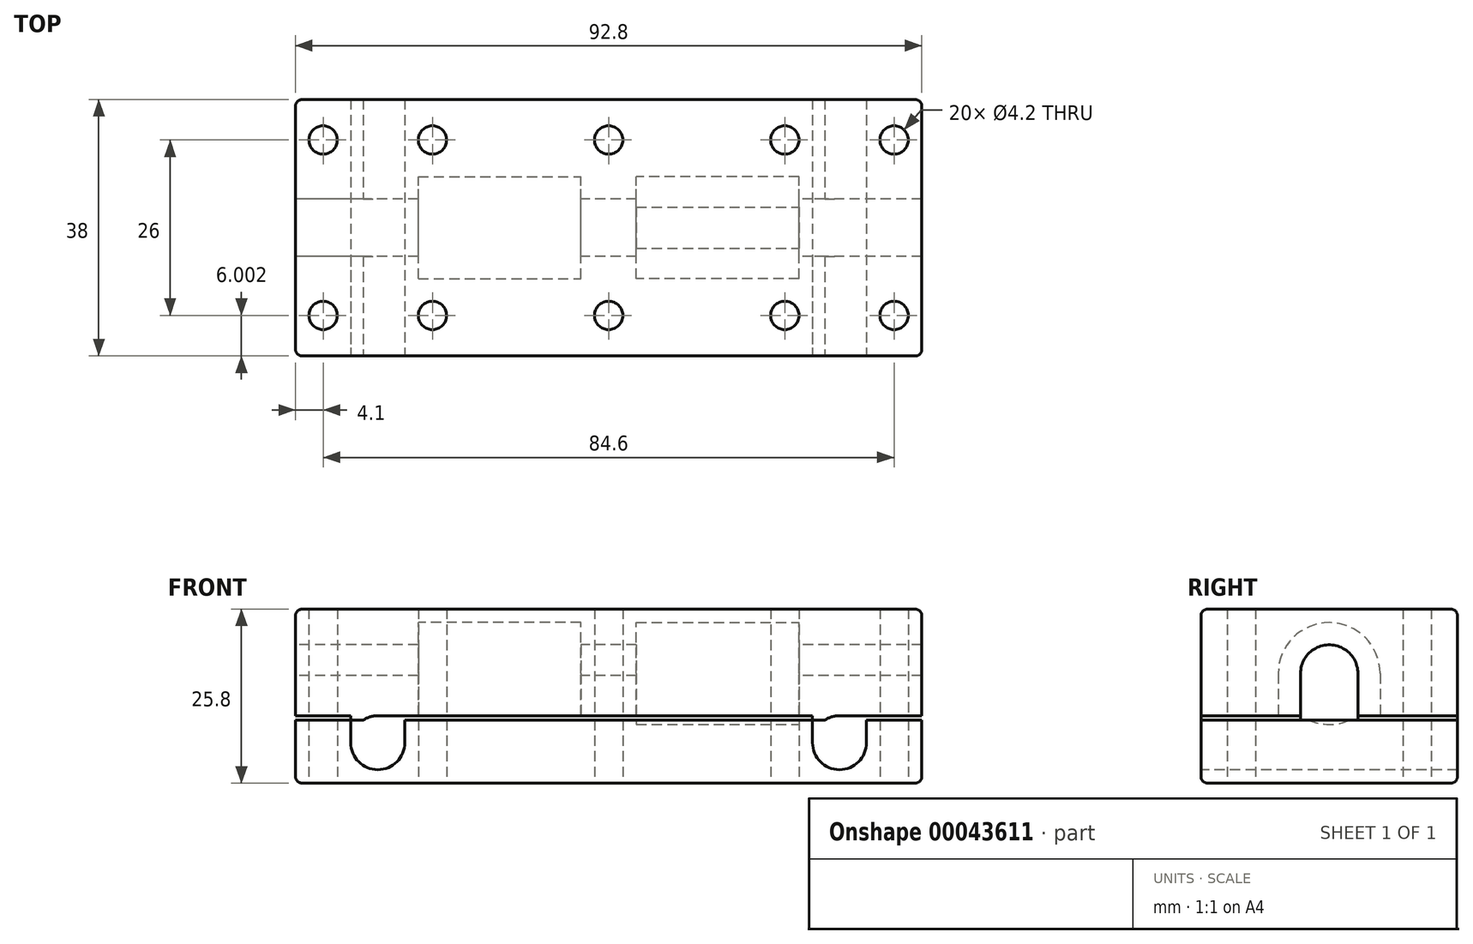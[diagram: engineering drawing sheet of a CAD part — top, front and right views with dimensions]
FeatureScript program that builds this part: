
annotation { "Feature Type Name" : "Feature", "Feature Type Description" : "" }
export const myFeature = defineFeature(function(context is Context, id is Id, definition is map)
    precondition{}
    {
        {
            var Q0;
            Q0=qCreatedBy(makeId("Top.planeOp"),FACE);
            var sketch = newSketch(context, id + "F0", { "sketchPlane" : qUnion([Q0])});
            skLineSegment(sketch, "E0.top", {"start": v(-94.16, -13.28) * mm, "end": v(-47.76, -13.28) * mm});
            skLineSegment(sketch, "E0.left", {"start": v(-94.16, 24.72) * mm, "end": v(-94.16, -13.28) * mm});
            skPoint(sketch, "E1", {"position": v(-94.16, 5.72) * mm});
            skLineSegment(sketch, "E2", {"start": v(-94.16, 5.72) * mm, "end": v(-47.76, 5.72) * mm, "construction": true});
            skPoint(sketch, "E3", {"position": v(-90.06, -13.28) * mm});
            skPoint(sketch, "E4", {"position": v(-81.96, -13.28) * mm});
            skPoint(sketch, "E5", {"position": v(-47.76, -13.28) * mm});
            skLineSegment(sketch, "E6.bottom", {"start": v(-75.96, 13.27) * mm, "end": v(-51.86, 13.27) * mm, "construction": true});
            skLineSegment(sketch, "E6.top", {"start": v(-75.96, -1.83) * mm, "end": v(-51.86, -1.83) * mm, "construction": true});
            skLineSegment(sketch, "E6.left", {"start": v(-75.96, 13.27) * mm, "end": v(-75.96, -1.83) * mm, "construction": true});
            skLineSegment(sketch, "E6.right", {"start": v(-51.86, 13.27) * mm, "end": v(-51.86, -1.83) * mm, "construction": true});
            skLineSegment(sketch, "E7.bottom", {"start": v(-85.96, -13.28) * mm, "end": v(-77.96, -13.28) * mm});
            skLineSegment(sketch, "E7.top", {"start": v(-85.96, 73.63) * mm, "end": v(-77.96, 73.63) * mm});
            skLineSegment(sketch, "E7.left", {"start": v(-85.96, -13.28) * mm, "end": v(-85.96, 73.63) * mm, "construction": true});
            skLineSegment(sketch, "E7.right", {"start": v(-77.96, -13.28) * mm, "end": v(-77.96, 73.63) * mm, "construction": true});
            skLineSegment(sketch, "E8", {"start": v(-47.76, -13.28) * mm, "end": v(-47.76, 24.72) * mm});
            skLineSegment(sketch, "E9", {"start": v(-94.16, 24.72) * mm, "end": v(-47.76, 24.72) * mm});
            skLineSegment(sketch, "E10.MirrorCS", {"start": v(-9.56, 73.63) * mm, "end": v(-17.56, 73.63) * mm});
            skLineSegment(sketch, "E11.MirrorCS", {"start": v(-9.56, -13.28) * mm, "end": v(-17.56, -13.28) * mm});
            skLineSegment(sketch, "E12.MirrorCS", {"start": v(-17.56, -13.28) * mm, "end": v(-17.56, 73.63) * mm, "construction": true});
            skLineSegment(sketch, "E13.MirrorCS", {"start": v(-1.36, 24.72) * mm, "end": v(-47.76, 24.72) * mm});
            skLineSegment(sketch, "E14.MirrorCS", {"start": v(-9.56, -13.28) * mm, "end": v(-9.56, 73.63) * mm, "construction": true});
            skPoint(sketch, "E15.MirrorP", {"position": v(-5.46, -13.28) * mm});
            skPoint(sketch, "E16.MirrorP", {"position": v(-13.56, -13.28) * mm});
            skLineSegment(sketch, "E17.MirrorCS", {"start": v(-1.36, 5.72) * mm, "end": v(-47.76, 5.72) * mm, "construction": true});
            skLineSegment(sketch, "E18.MirrorCS", {"start": v(-19.56, 13.27) * mm, "end": v(-43.66, 13.27) * mm, "construction": true});
            skLineSegment(sketch, "E19.MirrorCS", {"start": v(-19.56, -1.83) * mm, "end": v(-43.66, -1.83) * mm, "construction": true});
            skLineSegment(sketch, "E20.MirrorCS", {"start": v(-19.56, 13.27) * mm, "end": v(-19.56, -1.83) * mm, "construction": true});
            skLineSegment(sketch, "E21.MirrorCS", {"start": v(-43.66, 13.27) * mm, "end": v(-43.66, -1.83) * mm, "construction": true});
            skPoint(sketch, "E22.MirrorP", {"position": v(-1.36, 5.72) * mm});
            skLineSegment(sketch, "E23.MirrorCS", {"start": v(-1.36, -13.28) * mm, "end": v(-47.76, -13.28) * mm});
            skLineSegment(sketch, "E24.MirrorCS", {"start": v(-1.36, 24.72) * mm, "end": v(-1.36, -13.28) * mm});
            skPoint(sketch, "E25", {"position": v(-90.06, 18.72) * mm});
            skPoint(sketch, "E26", {"position": v(-47.76, 18.72) * mm});
            skPoint(sketch, "E27", {"position": v(-5.46, 18.72) * mm});
            skPoint(sketch, "E28", {"position": v(-5.46, -7.28) * mm});
            skPoint(sketch, "E29", {"position": v(-47.76, -7.28) * mm});
            skPoint(sketch, "E30", {"position": v(-90.06, -7.28) * mm});
            skLineSegment(sketch, "E31", {"start": v(-76.94, 18.72) * mm, "end": v(-49.91, 18.72) * mm, "construction": true});
            skPoint(sketch, "E32", {"position": v(-73.86, 18.72) * mm});
            skPoint(sketch, "E33", {"position": v(-21.66, 18.72) * mm});
            skPoint(sketch, "E34", {"position": v(-73.86, -7.28) * mm});
            skPoint(sketch, "E35", {"position": v(-21.66, -7.28) * mm});
            skSolve(sketch);
        }
        {
            var Q0;
            {var subQ1=sQuery(id+"F0.wireOp",EDGE,"E0.left");Q0=makeQuery(id+"F0.imprint","IMPRINT",FACE,{"disambiguationData":[TD([[makeQuery(id+"F0.imprint","IMPRINT",EDGE,{"derivedFrom":subQ1}),1.0]])]});}
            var Q1;
            {var subQ0=sQuery(id+"F0.wireOp",EDGE,"E8");Q1=makeQuery(id+"F0.imprint","IMPRINT",FACE,{"disambiguationData":[TD([[makeQuery(id+"F0.imprint","IMPRINT",EDGE,{"derivedFrom":subQ0}),-1.0]])]});}
            extrude(context, id + "F1", {"entities" : qUnion([Q0, Q1]), "depth" : 25.8 * mm});
        }
        {
            var Q0;
            Q0=makeQuery(id+"F1.opExtrude","SWEPT_FACE",FACE,{"disambiguationData":[OSD([sQuery(id+"F0.wireOp",EDGE,"E0.left")])]});
            var sketch = newSketch(context, id + "F2", { "sketchPlane" : qUnion([Q0])});
            skPoint(sketch, "E36", {"position": v(-5.72, 16.25) * mm});
            skCircle(sketch, "E37", {"center": v(-5.72, 16.25) * mm, "radius": 4.25 * mm});
            skCircle(sketch, "E38", {"center": v(-5.72, 16.25) * mm, "radius": 7.55 * mm});
            skLineSegment(sketch, "E39", {"start": v(-24.72, 9.35) * mm, "end": v(13.28, 9.35) * mm});
            skLineSegment(sketch, "E40", {"start": v(-9.96, 15.96) * mm, "end": v(-9.96, 9.35) * mm});
            skLineSegment(sketch, "E41", {"start": v(-1.47, 16.25) * mm, "end": v(-1.47, 9.35) * mm});
            skPoint(sketch, "E42", {"position": v(-24.72, -4.75) * mm});
            skPoint(sketch, "E43", {"position": v(-24.72, -16.75) * mm});
            skSolve(sketch);
        }
        {
            var Q0;
            Q0=makeQuery(id+"F1.opExtrude","SWEPT_FACE",FACE,{"disambiguationData":[OSD([sQuery(id+"F0.wireOp",EDGE,"E0.top"),sQuery(id+"F0.wireOp",EDGE,"E7.bottom"),sQuery(id+"F0.wireOp",EDGE,"E23.MirrorCS")])]});
            var sketch = newSketch(context, id + "F3", { "sketchPlane" : qUnion([Q0])});
            skPoint(sketch, "E44", {"position": v(-81.96, 6) * mm});
            skCircle(sketch, "E45", {"center": v(-81.96, 6) * mm, "radius": 4 * mm});
            skPoint(sketch, "E46", {"position": v(-13.56, 6) * mm});
            skCircle(sketch, "E47", {"center": v(-13.56, 6) * mm, "radius": 4 * mm});
            skLineSegment(sketch, "E48.bottom", {"start": v(-94.16, 10) * mm, "end": v(-1.36, 10) * mm});
            skLineSegment(sketch, "E48.top", {"start": v(-94.16, 9.35) * mm, "end": v(-1.36, 9.35) * mm});
            skLineSegment(sketch, "E48.left", {"start": v(-94.16, 10) * mm, "end": v(-94.16, 9.35) * mm});
            skLineSegment(sketch, "E48.right", {"start": v(-1.36, 10) * mm, "end": v(-1.36, 9.35) * mm});
            skLineSegment(sketch, "E49.bottom", {"start": v(-85.96, 6) * mm, "end": v(-77.96, 6) * mm});
            skLineSegment(sketch, "E49.top", {"start": v(-85.96, 10) * mm, "end": v(-77.96, 10) * mm});
            skLineSegment(sketch, "E49.left", {"start": v(-85.96, 6) * mm, "end": v(-85.96, 10) * mm});
            skLineSegment(sketch, "E49.right", {"start": v(-77.96, 6) * mm, "end": v(-77.96, 10) * mm});
            skLineSegment(sketch, "E50.bottom", {"start": v(-17.56, 6) * mm, "end": v(-9.56, 6) * mm});
            skLineSegment(sketch, "E50.top", {"start": v(-17.56, 10) * mm, "end": v(-9.56, 10) * mm});
            skLineSegment(sketch, "E50.left", {"start": v(-17.56, 6) * mm, "end": v(-17.56, 10) * mm});
            skLineSegment(sketch, "E50.right", {"start": v(-9.56, 6) * mm, "end": v(-9.56, 10) * mm});
            skSolve(sketch);
        }
        {
            var Q0;
            Q0=makeQuery(id+"F2.imprint","IMPRINT",FACE,{"disambiguationData":[TD([[makeQuery(id+"F2.imprint","IMPRINT",EDGE,{"derivedFrom":sQuery(id+"F2.wireOp",EDGE,"E37")}),1.0]])]});
            var Q1;
            {var subQ6=sQuery(id+"F2.wireOp",EDGE,"E40");var subQ8=sQuery(id+"F2.wireOp",EDGE,"E37");var subQ9=makeQuery(id+"F2.imprint","INTERSECT",VERTEX,{"derivedFrom":[subQ8,subQ6]});Q1=makeQuery(id+"F2.imprint","IMPRINT",FACE,{"disambiguationData":[TD([[makeQuery(id+"F2.imprint","IMPRINT",EDGE,{"disambiguationData":[TD([[subQ9,-1.0]])],"derivedFrom":subQ8}),-1.0]])]});}
            var Q2;
            {var subQ0=sQuery(id+"F2.wireOp",EDGE,"E39");var subQ1=sQuery(id+"F2.wireOp",EDGE,"E38");var subQ2=makeQuery(id+"F2.imprint","INTERSECT",VERTEX,{"disambiguationData":[OD(0.0)],"derivedFrom":[subQ1,subQ0]});Q2=makeQuery(id+"F2.imprint","IMPRINT",FACE,{"disambiguationData":[TD([[makeQuery(id+"F2.imprint","IMPRINT",EDGE,{"disambiguationData":[TD([[subQ2,1.0]])],"derivedFrom":subQ1}),-1.0]])]});}
            var Q3;
            {var subQ0=sQuery(id+"F2.wireOp",EDGE,"E39");var subQ1=sQuery(id+"F2.wireOp",EDGE,"E38");var subQ2=makeQuery(id+"F2.imprint","INTERSECT",VERTEX,{"disambiguationData":[OD(1.0)],"derivedFrom":[subQ1,subQ0]});Q3=makeQuery(id+"F2.imprint","IMPRINT",FACE,{"disambiguationData":[TD([[makeQuery(id+"F2.imprint","IMPRINT",EDGE,{"disambiguationData":[TD([[subQ2,-1.0]])],"derivedFrom":subQ1}),-1.0]])]});}
            extrude(context, id + "F4", {"entities" : qUnion([Q0, Q1, Q2, Q3]), "operationType" : NewBodyOperationType.REMOVE, "endBound" : BoundingType.THROUGH_ALL, "oppositeDirection" : true, "depth" : 25 * mm});
        }
        {
            var Q0;
            Q0=makeQuery(id+"F3.imprint","IMPRINT",FACE,{"disambiguationData":[TD([[makeQuery(id+"F3.imprint","IMPRINT",EDGE,{"derivedFrom":sQuery(id+"F3.wireOp",EDGE,"E45")}),1.0]])]});
            var Q1;
            Q1=makeQuery(id+"F3.imprint","IMPRINT",FACE,{"disambiguationData":[TD([[makeQuery(id+"F3.imprint","IMPRINT",EDGE,{"derivedFrom":sQuery(id+"F3.wireOp",EDGE,"E47")}),1.0]])]});
            var Q2;
            {var subQ0=sQuery(id+"F3.wireOp",EDGE,"E49.bottom");Q2=makeQuery(id+"F3.imprint","IMPRINT",FACE,{"disambiguationData":[TD([[makeQuery(id+"F3.imprint","IMPRINT",EDGE,{"derivedFrom":subQ0}),1.0]])]});}
            var Q3;
            {var subQ0=sQuery(id+"F3.wireOp",EDGE,"E49.bottom");Q3=makeQuery(id+"F3.imprint","IMPRINT",FACE,{"disambiguationData":[TD([[makeQuery(id+"F3.imprint","IMPRINT",EDGE,{"derivedFrom":subQ0}),-1.0]])]});}
            var Q4;
            {var subQ1=sQuery(id+"F3.wireOp",EDGE,"E45");var subQ3=sQuery(id+"F3.wireOp",EDGE,"E48.top");var subQ4=makeQuery(id+"F3.imprint","INTERSECT",VERTEX,{"disambiguationData":[OD(0.0)],"derivedFrom":[subQ1,subQ3]});Q4=makeQuery(id+"F3.imprint","IMPRINT",FACE,{"disambiguationData":[TD([[makeQuery(id+"F3.imprint","IMPRINT",EDGE,{"disambiguationData":[TD([[subQ4,-1.0]])],"derivedFrom":subQ3}),-1.0]])]});}
            var Q5;
            {var subQ0=sQuery(id+"F3.wireOp",EDGE,"E48.top");var subQ1=sQuery(id+"F3.wireOp",EDGE,"E45");var subQ2=makeQuery(id+"F3.imprint","INTERSECT",VERTEX,{"disambiguationData":[OD(0.0)],"derivedFrom":[subQ1,subQ0]});Q5=makeQuery(id+"F3.imprint","IMPRINT",FACE,{"disambiguationData":[TD([[makeQuery(id+"F3.imprint","IMPRINT",EDGE,{"disambiguationData":[TD([[subQ2,-1.0]])],"derivedFrom":subQ1}),-1.0]])]});}
            var Q6;
            {var subQ0=sQuery(id+"F3.wireOp",EDGE,"E49.top");var subQ1=sQuery(id+"F3.wireOp",EDGE,"E45");var subQ2=makeQuery(id+"F3.imprint","INTERSECT",VERTEX,{"derivedFrom":[subQ1,subQ0]});Q6=makeQuery(id+"F3.imprint","IMPRINT",FACE,{"disambiguationData":[TD([[makeQuery(id+"F3.imprint","IMPRINT",EDGE,{"disambiguationData":[TD([[subQ2,-1.0]])],"derivedFrom":subQ1}),-1.0]])]});}
            var Q7;
            {var subQ1=sQuery(id+"F3.wireOp",EDGE,"E45");var subQ3=sQuery(id+"F3.wireOp",EDGE,"E48.top");var subQ4=makeQuery(id+"F3.imprint","INTERSECT",VERTEX,{"disambiguationData":[OD(1.0)],"derivedFrom":[subQ1,subQ3]});Q7=makeQuery(id+"F3.imprint","IMPRINT",FACE,{"disambiguationData":[TD([[makeQuery(id+"F3.imprint","IMPRINT",EDGE,{"disambiguationData":[TD([[subQ4,1.0]])],"derivedFrom":subQ3}),-1.0]])]});}
            var Q8;
            {var subQ0=sQuery(id+"F3.wireOp",EDGE,"E50.bottom");Q8=makeQuery(id+"F3.imprint","IMPRINT",FACE,{"disambiguationData":[TD([[makeQuery(id+"F3.imprint","IMPRINT",EDGE,{"derivedFrom":subQ0}),1.0]])]});}
            var Q9;
            {var subQ0=sQuery(id+"F3.wireOp",EDGE,"E50.bottom");Q9=makeQuery(id+"F3.imprint","IMPRINT",FACE,{"disambiguationData":[TD([[makeQuery(id+"F3.imprint","IMPRINT",EDGE,{"derivedFrom":subQ0}),-1.0]])]});}
            var Q10;
            {var subQ0=sQuery(id+"F3.wireOp",EDGE,"E50.top");var subQ1=sQuery(id+"F3.wireOp",EDGE,"E47");var subQ2=makeQuery(id+"F3.imprint","INTERSECT",VERTEX,{"derivedFrom":[subQ1,subQ0]});Q10=makeQuery(id+"F3.imprint","IMPRINT",FACE,{"disambiguationData":[TD([[makeQuery(id+"F3.imprint","IMPRINT",EDGE,{"disambiguationData":[TD([[subQ2,-1.0]])],"derivedFrom":subQ1}),-1.0]])]});}
            var Q11;
            {var subQ1=sQuery(id+"F3.wireOp",EDGE,"E47");var subQ3=sQuery(id+"F3.wireOp",EDGE,"E48.top");var subQ4=makeQuery(id+"F3.imprint","INTERSECT",VERTEX,{"disambiguationData":[OD(1.0)],"derivedFrom":[subQ1,subQ3]});Q11=makeQuery(id+"F3.imprint","IMPRINT",FACE,{"disambiguationData":[TD([[makeQuery(id+"F3.imprint","IMPRINT",EDGE,{"disambiguationData":[TD([[subQ4,1.0]])],"derivedFrom":subQ3}),-1.0]])]});}
            var Q12;
            {var subQ1=sQuery(id+"F3.wireOp",EDGE,"E47");var subQ3=sQuery(id+"F3.wireOp",EDGE,"E48.top");var subQ4=makeQuery(id+"F3.imprint","INTERSECT",VERTEX,{"disambiguationData":[OD(0.0)],"derivedFrom":[subQ1,subQ3]});Q12=makeQuery(id+"F3.imprint","IMPRINT",FACE,{"disambiguationData":[TD([[makeQuery(id+"F3.imprint","IMPRINT",EDGE,{"disambiguationData":[TD([[subQ4,-1.0]])],"derivedFrom":subQ3}),-1.0]])]});}
            var Q13;
            {var subQ0=sQuery(id+"F3.wireOp",EDGE,"E48.top");var subQ1=sQuery(id+"F3.wireOp",EDGE,"E47");var subQ2=makeQuery(id+"F3.imprint","INTERSECT",VERTEX,{"disambiguationData":[OD(0.0)],"derivedFrom":[subQ1,subQ0]});Q13=makeQuery(id+"F3.imprint","IMPRINT",FACE,{"disambiguationData":[TD([[makeQuery(id+"F3.imprint","IMPRINT",EDGE,{"disambiguationData":[TD([[subQ2,-1.0]])],"derivedFrom":subQ1}),-1.0]])]});}
            var Q14;
            {var subQ0=sQuery(id+"F3.wireOp",EDGE,"E49.right");var subQ5=sQuery(id+"F3.wireOp",EDGE,"E48.top");var subQ6=makeQuery(id+"F3.imprint","INTERSECT",VERTEX,{"derivedFrom":[subQ5,subQ0]});Q14=makeQuery(id+"F3.imprint","IMPRINT",FACE,{"disambiguationData":[TD([[makeQuery(id+"F3.imprint","IMPRINT",EDGE,{"disambiguationData":[TD([[subQ6,-1.0]])],"derivedFrom":subQ5}),1.0]])]});}
            var Q15;
            {var subQ0=sQuery(id+"F3.wireOp",EDGE,"E48.left");Q15=makeQuery(id+"F3.imprint","IMPRINT",FACE,{"disambiguationData":[TD([[makeQuery(id+"F3.imprint","IMPRINT",EDGE,{"derivedFrom":subQ0}),1.0]])]});}
            var Q16;
            {var subQ0=sQuery(id+"F3.wireOp",EDGE,"E48.right");Q16=makeQuery(id+"F3.imprint","IMPRINT",FACE,{"disambiguationData":[TD([[makeQuery(id+"F3.imprint","IMPRINT",EDGE,{"derivedFrom":subQ0}),-1.0]])]});}
            extrude(context, id + "F5", {"entities" : qUnion([Q0, Q1, Q2, Q3, Q4, Q5, Q6, Q7, Q8, Q9, Q10, Q11, Q12, Q13, Q14, Q15, Q16]), "operationType" : NewBodyOperationType.REMOVE, "endBound" : BoundingType.THROUGH_ALL, "oppositeDirection" : true, "depth" : 25 * mm});
        }
        {
            var Q0;
            Q0=sQuery(id+"F0.wireOp",EDGE,"E6.left");
            var Q1;
            Q1=qCreatedBy(makeId("Right.planeOp"),FACE);
            cPlane(context, id + "F6", {"entities" : qUnion([Q0, Q1]), "cplaneType" : CPlaneType.LINE_ANGLE, "offset" : 25 * mm, "angle" : 0 * degree, "width" : 150 * mm, "height" : 150 * mm});
        }
        {
            var Q0;
            Q0=qCreatedBy(id+"F6.planeOp",FACE);
            var sketch = newSketch(context, id + "F7", { "sketchPlane" : qUnion([Q0])});
            skCircle(sketch, "E51", {"center": v(-5.72, 16.25) * mm, "radius": 7.55 * mm});
            skLineSegment(sketch, "E52.bottom", {"start": v(-13.27, 16.25) * mm, "end": v(1.83, 16.25) * mm});
            skLineSegment(sketch, "E52.top", {"start": v(-13.27, 9.35) * mm, "end": v(1.83, 9.35) * mm});
            skLineSegment(sketch, "E52.left", {"start": v(-13.27, 16.25) * mm, "end": v(-13.27, 9.35) * mm});
            skLineSegment(sketch, "E52.right", {"start": v(1.83, 16.25) * mm, "end": v(1.83, 9.35) * mm});
            skSolve(sketch);
        }
        {
            var Q0;
            {var subQ0=sQuery(id+"F7.wireOp",EDGE,"E52.left");Q0=makeQuery(id+"F7.imprint","IMPRINT",FACE,{"disambiguationData":[TD([[makeQuery(id+"F7.imprint","IMPRINT",EDGE,{"derivedFrom":subQ0}),1.0]])]});}
            var Q1;
            {var subQ0=sQuery(id+"F7.wireOp",EDGE,"E52.right");Q1=makeQuery(id+"F7.imprint","IMPRINT",FACE,{"disambiguationData":[TD([[makeQuery(id+"F7.imprint","IMPRINT",EDGE,{"derivedFrom":subQ0}),-1.0]])]});}
            var Q2;
            {var subQ0=sQuery(id+"F7.wireOp",EDGE,"E52.bottom");Q2=makeQuery(id+"F7.imprint","IMPRINT",FACE,{"disambiguationData":[TD([[makeQuery(id+"F7.imprint","IMPRINT",EDGE,{"derivedFrom":subQ0}),-1.0]])]});}
            var Q3;
            {var subQ0=sQuery(id+"F7.wireOp",EDGE,"E52.bottom");Q3=makeQuery(id+"F7.imprint","IMPRINT",FACE,{"disambiguationData":[TD([[makeQuery(id+"F7.imprint","IMPRINT",EDGE,{"derivedFrom":subQ0}),1.0]])]});}
            var Q4;
            {var subQ0=sQuery(id+"F7.wireOp",EDGE,"E52.top");var subQ1=sQuery(id+"F7.wireOp",EDGE,"E51");var subQ2=makeQuery(id+"F7.imprint","INTERSECT",VERTEX,{"disambiguationData":[OD(0.0)],"derivedFrom":[subQ1,subQ0]});Q4=makeQuery(id+"F7.imprint","IMPRINT",FACE,{"disambiguationData":[TD([[makeQuery(id+"F7.imprint","IMPRINT",EDGE,{"disambiguationData":[TD([[subQ2,-1.0]])],"derivedFrom":subQ1}),1.0]])]});}
            extrude(context, id + "F8", {"entities" : qUnion([Q0, Q1, Q2, Q3, Q4]), "operationType" : NewBodyOperationType.REMOVE, "oppositeDirection" : true, "depth" : 24.1 * mm});
        }
        {
            var Q0;
            Q0=sQuery(id+"F0.wireOp",EDGE,"E20.MirrorCS");
            var Q1;
            Q1=qCreatedBy(makeId("Right.planeOp"),FACE);
            cPlane(context, id + "F9", {"entities" : qUnion([Q0, Q1]), "cplaneType" : CPlaneType.LINE_ANGLE, "offset" : 25 * mm, "angle" : 0 * degree, "width" : 150 * mm, "height" : 150 * mm});
        }
        {
            var Q0;
            Q0=qCreatedBy(id+"F9.planeOp",FACE);
            var sketch = newSketch(context, id + "F10", { "sketchPlane" : qUnion([Q0])});
            skPoint(sketch, "E53", {"position": v(-5.72, 16.25) * mm});
            skCircle(sketch, "E54", {"center": v(-5.72, 16.25) * mm, "radius": 7.55 * mm});
            skLineSegment(sketch, "E55.bottom", {"start": v(1.83, 16.25) * mm, "end": v(-13.27, 16.25) * mm});
            skLineSegment(sketch, "E55.top", {"start": v(1.83, 9.35) * mm, "end": v(-13.27, 9.35) * mm});
            skLineSegment(sketch, "E55.left", {"start": v(1.83, 16.25) * mm, "end": v(1.83, 9.35) * mm});
            skLineSegment(sketch, "E55.right", {"start": v(-13.27, 16.25) * mm, "end": v(-13.27, 9.35) * mm});
            skSolve(sketch);
        }
        {
            var Q0;
            {var subQ0=sQuery(id+"F10.wireOp",EDGE,"E55.bottom");Q0=makeQuery(id+"F10.imprint","IMPRINT",FACE,{"disambiguationData":[TD([[makeQuery(id+"F10.imprint","IMPRINT",EDGE,{"derivedFrom":subQ0}),-1.0]])]});}
            var Q1;
            {var subQ0=sQuery(id+"F10.wireOp",EDGE,"E55.bottom");Q1=makeQuery(id+"F10.imprint","IMPRINT",FACE,{"disambiguationData":[TD([[makeQuery(id+"F10.imprint","IMPRINT",EDGE,{"derivedFrom":subQ0}),1.0]])]});}
            var Q2;
            {var subQ0=sQuery(id+"F10.wireOp",EDGE,"E55.right");Q2=makeQuery(id+"F10.imprint","IMPRINT",FACE,{"disambiguationData":[TD([[makeQuery(id+"F10.imprint","IMPRINT",EDGE,{"derivedFrom":subQ0}),1.0]])]});}
            var Q3;
            {var subQ0=sQuery(id+"F10.wireOp",EDGE,"E55.left");Q3=makeQuery(id+"F10.imprint","IMPRINT",FACE,{"disambiguationData":[TD([[makeQuery(id+"F10.imprint","IMPRINT",EDGE,{"derivedFrom":subQ0}),-1.0]])]});}
            var Q4;
            {var subQ0=sQuery(id+"F10.wireOp",EDGE,"E55.top");var subQ1=sQuery(id+"F10.wireOp",EDGE,"E54");var subQ2=makeQuery(id+"F10.imprint","INTERSECT",VERTEX,{"disambiguationData":[OD(0.0)],"derivedFrom":[subQ1,subQ0]});Q4=makeQuery(id+"F10.imprint","IMPRINT",FACE,{"disambiguationData":[TD([[makeQuery(id+"F10.imprint","IMPRINT",EDGE,{"disambiguationData":[TD([[subQ2,-1.0]])],"derivedFrom":subQ1}),1.0]])]});}
            extrude(context, id + "F11", {"entities" : qUnion([Q0, Q1, Q2, Q3, Q4]), "operationType" : NewBodyOperationType.REMOVE, "depth" : 24.1 * mm});
        }
        {
            var Q0;
            Q0=makeQuery(id+"F1.opExtrude","CAP_EDGE",EDGE,{"disambiguationData":[OSD([sQuery(id+"F0.wireOp",EDGE,"E0.top"),sQuery(id+"F0.wireOp",EDGE,"E7.bottom"),sQuery(id+"F0.wireOp",EDGE,"E23.MirrorCS")])],"isStart":true});
            var Q1;
            Q1=makeQuery(id+"F1.opExtrude","CAP_EDGE",EDGE,{"disambiguationData":[OSD([sQuery(id+"F0.wireOp",EDGE,"E24.MirrorCS")])],"isStart":true});
            var Q2;
            Q2=makeQuery(id+"F1.opExtrude","CAP_EDGE",EDGE,{"disambiguationData":[OSD([sQuery(id+"F0.wireOp",EDGE,"E0.left")])],"isStart":true});
            var Q3;
            Q3=makeQuery(id+"F1.opExtrude","CAP_EDGE",EDGE,{"disambiguationData":[OSD([sQuery(id+"F0.wireOp",EDGE,"E9"),sQuery(id+"F0.wireOp",EDGE,"E13.MirrorCS")])],"isStart":false});
            var Q4;
            Q4=makeQuery(id+"F1.opExtrude","CAP_EDGE",EDGE,{"disambiguationData":[OSD([sQuery(id+"F0.wireOp",EDGE,"E0.top"),sQuery(id+"F0.wireOp",EDGE,"E7.bottom"),sQuery(id+"F0.wireOp",EDGE,"E23.MirrorCS")])],"isStart":false});
            var Q5;
            Q5=makeQuery(id+"F1.opExtrude","CAP_EDGE",EDGE,{"disambiguationData":[OSD([sQuery(id+"F0.wireOp",EDGE,"E24.MirrorCS")])],"isStart":false});
            var Q6;
            {var subQ0=sQuery(id+"F0.wireOp",EDGE,"E24.MirrorCS");var subQ1=sQuery(id+"F0.wireOp",EDGE,"E13.MirrorCS");Q6=makeQuery(id+"F5.boolean.opBoolean","SPLIT",EDGE,{"disambiguationData":[TD([makeQuery(id+"F5.opExtrude","SWEPT_FACE",FACE,{"disambiguationData":[OSD([sQuery(id+"F3.wireOp",EDGE,"E48.bottom"),sQuery(id+"F3.wireOp",EDGE,"E49.top"),sQuery(id+"F3.wireOp",EDGE,"E50.top")])]})])],"derivedFrom":makeQuery(id+"F1.opExtrude","SWEPT_EDGE",EDGE,{"disambiguationData":[OSD([subQ1,subQ0])]})});}
            var Q7;
            {var subQ0=sQuery(id+"F0.wireOp",EDGE,"E24.MirrorCS");var subQ1=sQuery(id+"F0.wireOp",EDGE,"E23.MirrorCS");Q7=makeQuery(id+"F5.boolean.opBoolean","SPLIT",EDGE,{"disambiguationData":[TD([makeQuery(id+"F5.opExtrude","SWEPT_FACE",FACE,{"disambiguationData":[OSD([sQuery(id+"F3.wireOp",EDGE,"E48.bottom"),sQuery(id+"F3.wireOp",EDGE,"E49.top"),sQuery(id+"F3.wireOp",EDGE,"E50.top")])]})])],"derivedFrom":makeQuery(id+"F1.opExtrude","SWEPT_EDGE",EDGE,{"disambiguationData":[OSD([subQ1,subQ0])]})});}
            var Q8;
            {var subQ0=sQuery(id+"F0.wireOp",EDGE,"E24.MirrorCS");var subQ1=sQuery(id+"F0.wireOp",EDGE,"E23.MirrorCS");var subQ5=makeQuery(id+"F1.opExtrude","SWEPT_EDGE",EDGE,{"disambiguationData":[OSD([subQ1,subQ0])]});Q8=makeQuery(id+"F5.boolean.opBoolean","SPLIT",EDGE,{"disambiguationData":[TD([makeQuery(id+"F4.boolean.opBoolean","COPY",FACE,{"derivedFrom":makeQuery(id+"F4.opExtrude","SWEPT_FACE",FACE,{"disambiguationData":[OSD([sQuery(id+"F2.wireOp",EDGE,"E39")])]})})])],"derivedFrom":subQ5});}
            var Q9;
            {var subQ0=sQuery(id+"F0.wireOp",EDGE,"E24.MirrorCS");var subQ1=sQuery(id+"F0.wireOp",EDGE,"E13.MirrorCS");Q9=makeQuery(id+"F5.boolean.opBoolean","SPLIT",EDGE,{"disambiguationData":[TD([makeQuery(id+"F4.boolean.opBoolean","COPY",FACE,{"derivedFrom":makeQuery(id+"F4.opExtrude","SWEPT_FACE",FACE,{"disambiguationData":[OSD([sQuery(id+"F2.wireOp",EDGE,"E39")])]})})])],"derivedFrom":makeQuery(id+"F1.opExtrude","SWEPT_EDGE",EDGE,{"disambiguationData":[OSD([subQ1,subQ0])]})});}
            var Q10;
            Q10=makeQuery(id+"F1.opExtrude","CAP_EDGE",EDGE,{"disambiguationData":[OSD([sQuery(id+"F0.wireOp",EDGE,"E0.left")])],"isStart":false});
            var Q11;
            {var subQ2=sQuery(id+"F0.wireOp",EDGE,"E0.left");var subQ3=sQuery(id+"F0.wireOp",EDGE,"E0.top");Q11=makeQuery(id+"F5.boolean.opBoolean","SPLIT",EDGE,{"disambiguationData":[TD([makeQuery(id+"F5.opExtrude","SWEPT_FACE",FACE,{"disambiguationData":[OSD([sQuery(id+"F3.wireOp",EDGE,"E48.bottom"),sQuery(id+"F3.wireOp",EDGE,"E49.top"),sQuery(id+"F3.wireOp",EDGE,"E50.top")])]})])],"derivedFrom":makeQuery(id+"F1.opExtrude","SWEPT_EDGE",EDGE,{"disambiguationData":[OSD([subQ3,subQ2])]})});}
            var Q12;
            {var subQ0=sQuery(id+"F0.wireOp",EDGE,"E0.left");var subQ3=sQuery(id+"F0.wireOp",EDGE,"E0.top");var subQ5=makeQuery(id+"F1.opExtrude","SWEPT_EDGE",EDGE,{"disambiguationData":[OSD([subQ3,subQ0])]});Q12=makeQuery(id+"F5.boolean.opBoolean","SPLIT",EDGE,{"disambiguationData":[TD([makeQuery(id+"F4.boolean.opBoolean","COPY",FACE,{"derivedFrom":makeQuery(id+"F4.opExtrude","SWEPT_FACE",FACE,{"disambiguationData":[OSD([sQuery(id+"F2.wireOp",EDGE,"E39")])]})})])],"derivedFrom":subQ5});}
            var Q13;
            {var subQ1=sQuery(id+"F0.wireOp",EDGE,"E9");var subQ3=sQuery(id+"F0.wireOp",EDGE,"E0.left");Q13=makeQuery(id+"F5.boolean.opBoolean","SPLIT",EDGE,{"disambiguationData":[TD([makeQuery(id+"F4.boolean.opBoolean","COPY",FACE,{"derivedFrom":makeQuery(id+"F4.opExtrude","SWEPT_FACE",FACE,{"disambiguationData":[OSD([sQuery(id+"F2.wireOp",EDGE,"E39")])]})})])],"derivedFrom":makeQuery(id+"F1.opExtrude","SWEPT_EDGE",EDGE,{"disambiguationData":[OSD([subQ3,subQ1])]})});}
            var Q14;
            {var subQ1=sQuery(id+"F0.wireOp",EDGE,"E9");var subQ2=sQuery(id+"F0.wireOp",EDGE,"E0.left");Q14=makeQuery(id+"F5.boolean.opBoolean","SPLIT",EDGE,{"disambiguationData":[TD([makeQuery(id+"F5.opExtrude","SWEPT_FACE",FACE,{"disambiguationData":[OSD([sQuery(id+"F3.wireOp",EDGE,"E48.bottom"),sQuery(id+"F3.wireOp",EDGE,"E49.top"),sQuery(id+"F3.wireOp",EDGE,"E50.top")])]})])],"derivedFrom":makeQuery(id+"F1.opExtrude","SWEPT_EDGE",EDGE,{"disambiguationData":[OSD([subQ2,subQ1])]})});}
            var Q15;
            {var subQ1=sQuery(id+"F0.wireOp",EDGE,"E24.MirrorCS");var subQ2=sQuery(id+"F0.wireOp",EDGE,"E13.MirrorCS");var subQ3=sQuery(id+"F0.wireOp",EDGE,"E9");Q15=makeQuery(id+"FaV5U625bywUatc_3.opBoolean","SPLIT",EDGE,{"disambiguationData":[TD([makeQuery(id+"F1.opExtrude","SWEPT_FACE",FACE,{"disambiguationData":[OSD([subQ1])]})])],"derivedFrom":makeQuery(id+"F1.opExtrude","CAP_EDGE",EDGE,{"disambiguationData":[OSD([subQ3,subQ2])],"isStart":true})});}
            var Q16;
            {var subQ0=sQuery(id+"Fnf9aDBOugkyyxO_1.wireOp",EDGE,"qgUEgUuF-Gk1c-hbKn-L9CV-MhQixRefJ1HH.right");var subQ1=sQuery(id+"F0.wireOp",EDGE,"E13.MirrorCS");var subQ2=sQuery(id+"F0.wireOp",EDGE,"E9");Q16=makeQuery(id+"FaV5U625bywUatc_3.opBoolean","SPLIT",EDGE,{"disambiguationData":[TD([makeQuery(id+"Fpmijf7J7eOStOP_1.opExtrude","SWEPT_FACE",FACE,{"disambiguationData":[OSD([subQ0])]})])],"derivedFrom":makeQuery(id+"F1.opExtrude","CAP_EDGE",EDGE,{"disambiguationData":[OSD([subQ2,subQ1])],"isStart":true})});}
            var Q17;
            {var subQ0=sQuery(id+"F0.wireOp",EDGE,"E13.MirrorCS");var subQ1=sQuery(id+"F0.wireOp",EDGE,"E9");var subQ2=sQuery(id+"F0.wireOp",EDGE,"E0.left");Q17=makeQuery(id+"FaV5U625bywUatc_3.opBoolean","SPLIT",EDGE,{"disambiguationData":[TD([makeQuery(id+"F1.opExtrude","SWEPT_FACE",FACE,{"disambiguationData":[OSD([subQ2])]})])],"derivedFrom":makeQuery(id+"F1.opExtrude","CAP_EDGE",EDGE,{"disambiguationData":[OSD([subQ1,subQ0])],"isStart":true})});}
            var Q18;
            Q18=makeQuery(id+"Fpmijf7J7eOStOP_1.opExtrude","CAP_EDGE",EDGE,{"disambiguationData":[OSD([sQuery(id+"Fnf9aDBOugkyyxO_1.wireOp",EDGE,"qgUEgUuF-Gk1c-hbKn-L9CV-MhQixRefJ1HH.right")])],"isStart":true});
            var Q19;
            Q19=makeQuery(id+"Fpmijf7J7eOStOP_1.opExtrude","CAP_EDGE",EDGE,{"disambiguationData":[OSD([sQuery(id+"Fnf9aDBOugkyyxO_1.wireOp",EDGE,"qgUEgUuF-Gk1c-hbKn-L9CV-MhQixRefJ1HH.left")])],"isStart":true});
            var Q20;
            Q20=makeQuery(id+"Fpmijf7J7eOStOP_1.opExtrude","CAP_EDGE",EDGE,{"disambiguationData":[OSD([sQuery(id+"Fnf9aDBOugkyyxO_1.wireOp",EDGE,"NabVYCMb-Tm3S-olCG-uXK1-GjPfyn5VKO74.left")])],"isStart":true});
            var Q21;
            Q21=makeQuery(id+"Fpmijf7J7eOStOP_1.opExtrude","CAP_EDGE",EDGE,{"disambiguationData":[OSD([sQuery(id+"Fnf9aDBOugkyyxO_1.wireOp",EDGE,"NabVYCMb-Tm3S-olCG-uXK1-GjPfyn5VKO74.right")])],"isStart":true});
            var Q22;
            Q22=makeQuery(id+"Fpmijf7J7eOStOP_1.opExtrude","SWEPT_EDGE",EDGE,{"disambiguationData":[OSD([sQuery(id+"F0.wireOp",EDGE,"E9"),sQuery(id+"F0.wireOp",EDGE,"E13.MirrorCS"),sQuery(id+"Fnf9aDBOugkyyxO_1.wireOp",EDGE,"qgUEgUuF-Gk1c-hbKn-L9CV-MhQixRefJ1HH.bottom"),sQuery(id+"Fnf9aDBOugkyyxO_1.wireOp",EDGE,"qgUEgUuF-Gk1c-hbKn-L9CV-MhQixRefJ1HH.right")])]});
            var Q23;
            Q23=makeQuery(id+"Fpmijf7J7eOStOP_1.opExtrude","CAP_EDGE",EDGE,{"disambiguationData":[OSD([sQuery(id+"Fnf9aDBOugkyyxO_1.wireOp",EDGE,"qgUEgUuF-Gk1c-hbKn-L9CV-MhQixRefJ1HH.bottom")])],"isStart":false});
            var Q24;
            Q24=makeQuery(id+"Fpmijf7J7eOStOP_1.opExtrude","CAP_EDGE",EDGE,{"disambiguationData":[OSD([sQuery(id+"Fnf9aDBOugkyyxO_1.wireOp",EDGE,"qgUEgUuF-Gk1c-hbKn-L9CV-MhQixRefJ1HH.left")])],"isStart":false});
            var Q25;
            Q25=makeQuery(id+"Fpmijf7J7eOStOP_1.opExtrude","CAP_EDGE",EDGE,{"disambiguationData":[OSD([sQuery(id+"Fnf9aDBOugkyyxO_1.wireOp",EDGE,"qgUEgUuF-Gk1c-hbKn-L9CV-MhQixRefJ1HH.right")])],"isStart":false});
            var Q26;
            Q26=makeQuery(id+"Fpmijf7J7eOStOP_1.opExtrude","CAP_EDGE",EDGE,{"disambiguationData":[OSD([sQuery(id+"Fnf9aDBOugkyyxO_1.wireOp",EDGE,"NabVYCMb-Tm3S-olCG-uXK1-GjPfyn5VKO74.left")])],"isStart":false});
            var Q27;
            Q27=makeQuery(id+"Fpmijf7J7eOStOP_1.opExtrude","CAP_EDGE",EDGE,{"disambiguationData":[OSD([sQuery(id+"Fnf9aDBOugkyyxO_1.wireOp",EDGE,"NabVYCMb-Tm3S-olCG-uXK1-GjPfyn5VKO74.right")])],"isStart":false});
            var Q28;
            Q28=makeQuery(id+"Fpmijf7J7eOStOP_1.opExtrude","CAP_EDGE",EDGE,{"disambiguationData":[OSD([sQuery(id+"Fnf9aDBOugkyyxO_1.wireOp",EDGE,"NabVYCMb-Tm3S-olCG-uXK1-GjPfyn5VKO74.top")])],"isStart":false});
            var Q29;
            Q29=makeQuery(id+"Fpmijf7J7eOStOP_1.opExtrude","CAP_EDGE",EDGE,{"disambiguationData":[OSD([sQuery(id+"Fnf9aDBOugkyyxO_1.wireOp",EDGE,"NabVYCMb-Tm3S-olCG-uXK1-GjPfyn5VKO74.bottom")])],"isStart":false});
            var Q30;
            Q30=makeQuery(id+"Fpmijf7J7eOStOP_1.opExtrude","SWEPT_EDGE",EDGE,{"disambiguationData":[OSD([sQuery(id+"Fnf9aDBOugkyyxO_1.wireOp",EDGE,"NabVYCMb-Tm3S-olCG-uXK1-GjPfyn5VKO74.bottom"),sQuery(id+"Fnf9aDBOugkyyxO_1.wireOp",EDGE,"NabVYCMb-Tm3S-olCG-uXK1-GjPfyn5VKO74.right")])]});
            var Q31;
            Q31=makeQuery(id+"Fpmijf7J7eOStOP_1.opExtrude","CAP_EDGE",EDGE,{"disambiguationData":[OSD([sQuery(id+"Fnf9aDBOugkyyxO_1.wireOp",EDGE,"NabVYCMb-Tm3S-olCG-uXK1-GjPfyn5VKO74.bottom")])],"isStart":true});
            var Q32;
            Q32=makeQuery(id+"Fpmijf7J7eOStOP_1.opExtrude","SWEPT_EDGE",EDGE,{"disambiguationData":[OSD([sQuery(id+"Fnf9aDBOugkyyxO_1.wireOp",EDGE,"NabVYCMb-Tm3S-olCG-uXK1-GjPfyn5VKO74.bottom"),sQuery(id+"Fnf9aDBOugkyyxO_1.wireOp",EDGE,"NabVYCMb-Tm3S-olCG-uXK1-GjPfyn5VKO74.left")])]});
            var Q33;
            Q33=makeQuery(id+"Fpmijf7J7eOStOP_1.opExtrude","SWEPT_EDGE",EDGE,{"disambiguationData":[OSD([sQuery(id+"Fnf9aDBOugkyyxO_1.wireOp",EDGE,"qgUEgUuF-Gk1c-hbKn-L9CV-MhQixRefJ1HH.top"),sQuery(id+"Fnf9aDBOugkyyxO_1.wireOp",EDGE,"qgUEgUuF-Gk1c-hbKn-L9CV-MhQixRefJ1HH.left")])]});
            var Q34;
            Q34=makeQuery(id+"Fpmijf7J7eOStOP_1.opExtrude","CAP_EDGE",EDGE,{"disambiguationData":[OSD([sQuery(id+"Fnf9aDBOugkyyxO_1.wireOp",EDGE,"qgUEgUuF-Gk1c-hbKn-L9CV-MhQixRefJ1HH.top")])],"isStart":true});
            var Q35;
            Q35=makeQuery(id+"Fpmijf7J7eOStOP_1.opExtrude","CAP_EDGE",EDGE,{"disambiguationData":[OSD([sQuery(id+"Fnf9aDBOugkyyxO_1.wireOp",EDGE,"qgUEgUuF-Gk1c-hbKn-L9CV-MhQixRefJ1HH.top")])],"isStart":false});
            var Q36;
            Q36=makeQuery(id+"Fpmijf7J7eOStOP_1.opExtrude","SWEPT_EDGE",EDGE,{"disambiguationData":[OSD([sQuery(id+"Fnf9aDBOugkyyxO_1.wireOp",EDGE,"qgUEgUuF-Gk1c-hbKn-L9CV-MhQixRefJ1HH.top"),sQuery(id+"Fnf9aDBOugkyyxO_1.wireOp",EDGE,"qgUEgUuF-Gk1c-hbKn-L9CV-MhQixRefJ1HH.right")])]});
            fillet(context, id + "F12", {"entities" : qUnion([Q0, Q1, Q2, Q3, Q4, Q5, Q6, Q7, Q8, Q9, Q10, Q11, Q12, Q13, Q14, Q15, Q16, Q17, Q18, Q19, Q20, Q21, Q22, Q23, Q24, Q25, Q26, Q27, Q28, Q29, Q30, Q31, Q32, Q33, Q34, Q35, Q36]), "radius" : 1 * mm, "tangentPropagation" : true, "allowEdgeOverflow" : false});
        }
        {
            var Q0;
            Q0=sQuery(id+"F0.wireOp",VERTEX,"E26");
            var Q1;
            Q1=sQuery(id+"F0.wireOp",VERTEX,"E29");
            var Q2;
            Q2=sQuery(id+"F0.wireOp",VERTEX,"E30");
            var Q3;
            Q3=sQuery(id+"F0.wireOp",VERTEX,"E28");
            var Q4;
            Q4=sQuery(id+"F0.wireOp",VERTEX,"E27");
            var Q5;
            Q5=sQuery(id+"F0.wireOp",VERTEX,"E33");
            var Q6;
            Q6=sQuery(id+"F0.wireOp",VERTEX,"E32");
            var Q7;
            Q7=sQuery(id+"F0.wireOp",VERTEX,"E25");
            var Q8;
            Q8=sQuery(id+"F0.wireOp",VERTEX,"E34");
            var Q9;
            Q9=sQuery(id+"F0.wireOp",VERTEX,"E35");
            var Q10;
            Q10=makeQuery(id+"F5.boolean.opBoolean","SPLIT",BODY,{"disambiguationData":[OD(1.0)],"derivedFrom":makeQuery(id+"F1.opExtrude","SWEPT_BODY",BODY,{"disambiguationData":[OSD([sQuery(id+"F0.wireOp",EDGE,"E0.top"),sQuery(id+"F0.wireOp",EDGE,"E0.left"),sQuery(id+"F0.wireOp",EDGE,"E7.bottom"),sQuery(id+"F0.wireOp",EDGE,"E9"),sQuery(id+"F0.wireOp",EDGE,"E13.MirrorCS"),sQuery(id+"F0.wireOp",EDGE,"E23.MirrorCS"),sQuery(id+"F0.wireOp",EDGE,"E24.MirrorCS")])]})});
            var Q11;
            Q11=makeQuery(id+"F5.boolean.opBoolean","SPLIT",BODY,{"disambiguationData":[OD(0.0)],"derivedFrom":makeQuery(id+"F1.opExtrude","SWEPT_BODY",BODY,{"disambiguationData":[OSD([sQuery(id+"F0.wireOp",EDGE,"E0.top"),sQuery(id+"F0.wireOp",EDGE,"E0.left"),sQuery(id+"F0.wireOp",EDGE,"E7.bottom"),sQuery(id+"F0.wireOp",EDGE,"E9"),sQuery(id+"F0.wireOp",EDGE,"E13.MirrorCS"),sQuery(id+"F0.wireOp",EDGE,"E23.MirrorCS"),sQuery(id+"F0.wireOp",EDGE,"E24.MirrorCS")])]})});
            hole(context, id + "F13", {"style" : HoleStyle.SIMPLE, "endStyle" : HoleEndStyle.THROUGH, "oppositeDirection" : true, "holeDiameter" : 4.2 * mm, "locations" : qUnion([Q0, Q1, Q2, Q3, Q4, Q5, Q6, Q7, Q8, Q9]), "scope" : qUnion([Q10, Q11]), "isTappedThrough" : true});
        }
    });
